# Revit family: Electrical_Equipment-Floor_Box-Hubbell_Wiring-1_Gang-Rectangular_Metal_Cover-PFBRG1
name_source: partatom
category: Electrical Fixtures
revit_build: Autodesk Revit 2015 (Build: 20140606_1530(x64)
units: mm (PartAtom-declared; Revit-internal decimal feet)

## types (1)
- PFBRG1 - 1 Gang - Metal Cover
    Adapter Frame Part Number = S5017G / SA5017G
    Adapter Ring Part Number = PFBRAC
    Assembly Code = D5020115
    Can Material = Non_Metallic-Hubbell-Plastic
    Conduit Connector 1 Radius = 0' - 0 5/8"
    Conduit Connector_1 Description = Conduit 1.25in. Connection
    Conduit Connector_2 Description = Conduit 1.25in. Connection
    Conduit Connector_3 Description = Conduit 1.25in. Connection
    Conduit Connector_4 Description = Conduit 1.25in. Connection
    Cover Material = Metal-Hubbell-Brass
    Default Elevation = 0' - 0"
    Description = Flush Rectangular Non-Metallic Concrete Floor Box with Metal Cover
    Floor Box Type = Non_Metallic Concrete Floor Box : PFBRG1 - Non_Metallic Concrete Floor Box
    Manufacturer = Hubbell-Wiring
    Model = PFBRG1
    Product Documentation Link = http://ecatalog.hubbell-wiring.com
    Product Page URL = http://ecatalog.hubbell-wiring.com
    Product data url = https://bimobject.com
    URL = http://www.hubbell-wiring.com

## geometry (parser evidence)
native form markers: Blend x21, Sweep x8
no freeform markers — native parametric forms only
